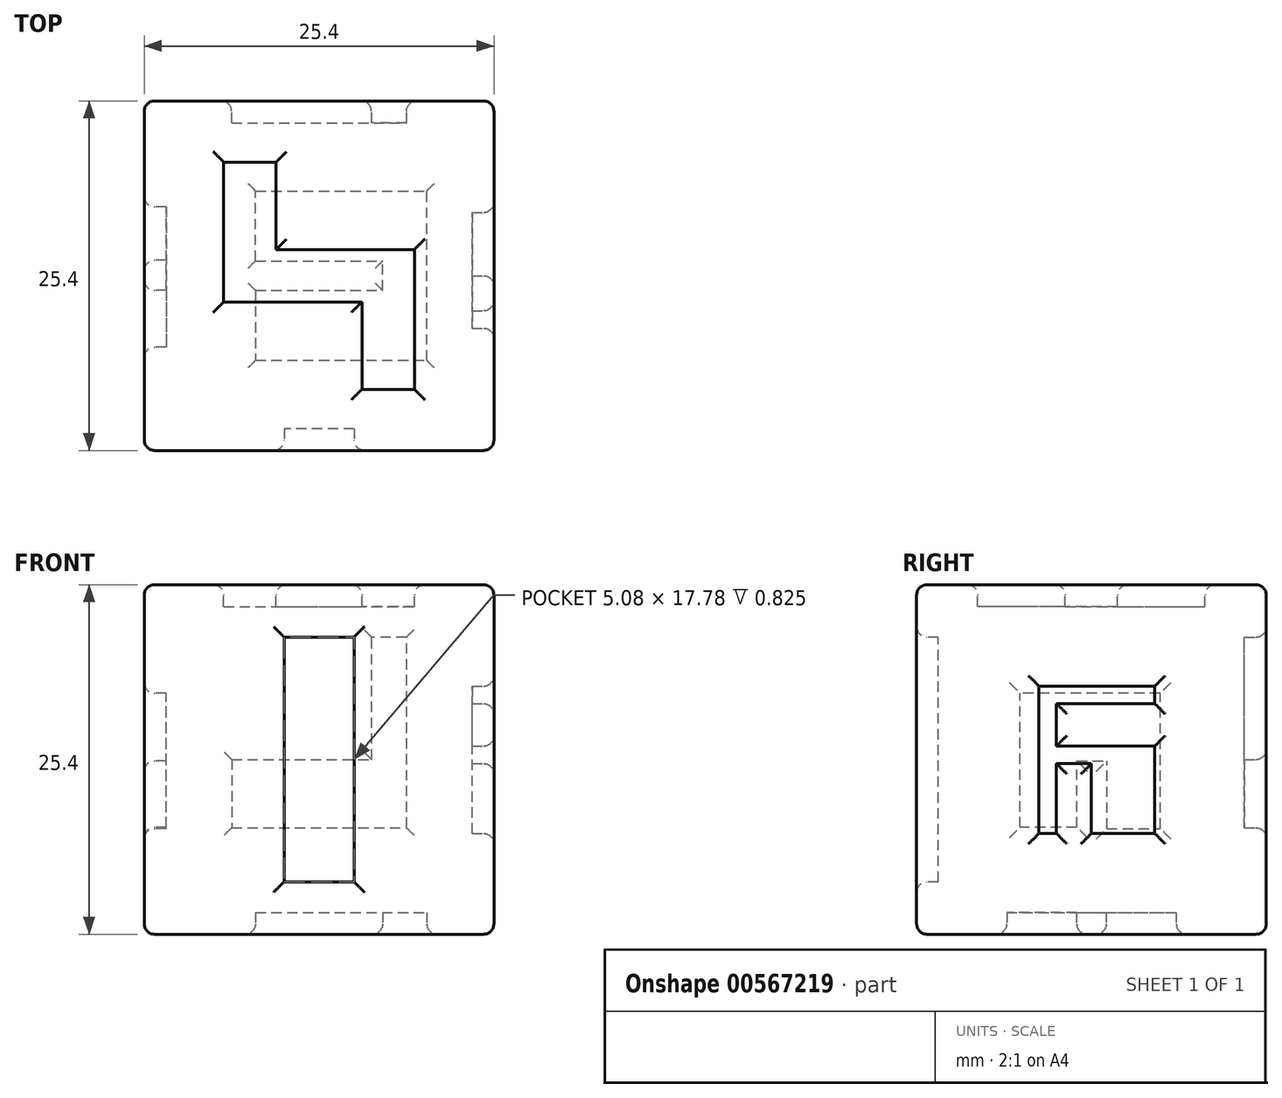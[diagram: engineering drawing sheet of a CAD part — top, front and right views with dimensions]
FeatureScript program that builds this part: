
annotation { "Feature Type Name" : "Feature", "Feature Type Description" : "" }
export const myFeature = defineFeature(function(context is Context, id is Id, definition is map)
    precondition{}
    {
        {
            var Q0;
            Q0=qCreatedBy(makeId("Top.planeOp"),FACE);
            var sketch = newSketch(context, id + "F0", { "sketchPlane" : qUnion([Q0])});
            skLineSegment(sketch, "E0.bottom", {"start": v(12.7, -12.7) * mm, "end": v(-12.7, -12.7) * mm});
            skLineSegment(sketch, "E0.top", {"start": v(12.7, 12.7) * mm, "end": v(-12.7, 12.7) * mm});
            skLineSegment(sketch, "E0.left", {"start": v(12.7, -12.7) * mm, "end": v(12.7, 12.7) * mm});
            skLineSegment(sketch, "E0.right", {"start": v(-12.7, -12.7) * mm, "end": v(-12.7, 12.7) * mm});
            skPoint(sketch, "E0.middle", {"position": v(0, 0) * mm});
            skSolve(sketch);
        }
        {
            var Q0;
            Q0=makeQuery(id+"F0.imprint","IMPRINT",FACE,{"disambiguationData":[TD([[makeQuery(id+"F0.imprint","IMPRINT",EDGE,{"derivedFrom":sQuery(id+"F0.wireOp",EDGE,"E0.bottom")}),-1.0]])]});
            extrude(context, id + "F1", {"entities" : qUnion([Q0]), "depth" : 25.4 * mm, "offsetDistance" : 25.4 * mm});
        }
        {
            var Q0;
            Q0=makeQuery(id+"F1.opExtrude","SWEPT_FACE",FACE,{"disambiguationData":[OSD([sQuery(id+"F0.wireOp",EDGE,"E0.bottom")])]});
            var sketch = newSketch(context, id + "F2", { "sketchPlane" : qUnion([Q0])});
            skLineSegment(sketch, "E1.bottom", {"start": v(2.54, 3.8) * mm, "end": v(-2.54, 3.8) * mm});
            skLineSegment(sketch, "E1.top", {"start": v(2.54, 21.59) * mm, "end": v(-2.54, 21.59) * mm});
            skLineSegment(sketch, "E1.left", {"start": v(2.54, 3.8) * mm, "end": v(2.54, 21.59) * mm});
            skLineSegment(sketch, "E1.right", {"start": v(-2.54, 3.8) * mm, "end": v(-2.54, 21.59) * mm});
            skPoint(sketch, "E1.middle", {"position": v(0, 12.7) * mm});
            skPoint(sketch, "E1.middle.positionSnap0", {"position": v(12.7, 12.7) * mm});
            skPoint(sketch, "E1.middle.positionSnap1", {"position": v(0, 0) * mm});
            skPoint(sketch, "E1.centerSnap0", {"position": v(12.7, 12.7) * mm});
            skPoint(sketch, "E1.centerSnap1", {"position": v(0, 0) * mm});
            skSolve(sketch);
        }
        {
            var Q0;
            Q0=makeQuery(id+"F1.opExtrude","CAP_FACE",FACE,{"disambiguationData":[OSD([sQuery(id+"F0.wireOp",EDGE,"E0.bottom"),sQuery(id+"F0.wireOp",EDGE,"E0.top"),sQuery(id+"F0.wireOp",EDGE,"E0.left"),sQuery(id+"F0.wireOp",EDGE,"E0.right")])],"isStart":false});
            var sketch = newSketch(context, id + "F3", { "sketchPlane" : qUnion([Q0])});
            skLineSegment(sketch, "E2.bottom", {"start": v(-6.93, -1.9) * mm, "end": v(3.12, -1.9) * mm});
            skLineSegment(sketch, "E2.top", {"start": v(-3.12, 1.9) * mm, "end": v(6.93, 1.9) * mm});
            skLineSegment(sketch, "E2.left", {"start": v(-6.93, -1.9) * mm, "end": v(-6.93, 1.9) * mm});
            skLineSegment(sketch, "E2.right", {"start": v(6.93, -1.9) * mm, "end": v(6.93, 1.9) * mm});
            skPoint(sketch, "E2.middle", {"position": v(0, 0) * mm});
            skLineSegment(sketch, "E3.top", {"start": v(-6.93, 8.26) * mm, "end": v(-3.12, 8.26) * mm});
            skLineSegment(sketch, "E3.left", {"start": v(-6.93, 1.9) * mm, "end": v(-6.93, 8.26) * mm});
            skLineSegment(sketch, "E3.right", {"start": v(-3.12, 1.9) * mm, "end": v(-3.12, 8.26) * mm});
            skLineSegment(sketch, "E4.top", {"start": v(6.93, -8.26) * mm, "end": v(3.12, -8.26) * mm});
            skLineSegment(sketch, "E4.left", {"start": v(6.93, -1.9) * mm, "end": v(6.93, -8.26) * mm});
            skLineSegment(sketch, "E4.right", {"start": v(3.12, -1.9) * mm, "end": v(3.12, -8.26) * mm});
            skSolve(sketch);
        }
        {
            var Q0;
            Q0=makeQuery(id+"F1.opExtrude","SWEPT_FACE",FACE,{"disambiguationData":[OSD([sQuery(id+"F0.wireOp",EDGE,"E0.top")])]});
            var sketch = newSketch(context, id + "F4", { "sketchPlane" : qUnion([Q0])});
            skPoint(sketch, "E5.firstSnap0", {"position": v(12.7, 12.7) * mm});
            skLineSegment(sketch, "E5.bottom", {"start": v(6.35, 12.7) * mm, "end": v(-3.81, 12.7) * mm});
            skLineSegment(sketch, "E5.top", {"start": v(6.35, 7.74) * mm, "end": v(-6.35, 7.74) * mm});
            skLineSegment(sketch, "E5.left", {"start": v(6.35, 12.7) * mm, "end": v(6.35, 7.74) * mm});
            skLineSegment(sketch, "E5.right", {"start": v(-6.35, 12.7) * mm, "end": v(-6.35, 7.74) * mm});
            skLineSegment(sketch, "E6.top", {"start": v(-6.35, 21.6) * mm, "end": v(-3.81, 21.6) * mm});
            skLineSegment(sketch, "E6.left", {"start": v(-6.35, 12.7) * mm, "end": v(-6.35, 21.6) * mm});
            skLineSegment(sketch, "E6.right", {"start": v(-3.81, 12.7) * mm, "end": v(-3.81, 21.6) * mm});
            skSolve(sketch);
        }
        {
            var Q0;
            Q0=makeQuery(id+"F1.opExtrude","CAP_FACE",FACE,{"disambiguationData":[OSD([sQuery(id+"F0.wireOp",EDGE,"E0.bottom"),sQuery(id+"F0.wireOp",EDGE,"E0.top"),sQuery(id+"F0.wireOp",EDGE,"E0.left"),sQuery(id+"F0.wireOp",EDGE,"E0.right")])],"isStart":true});
            var sketch = newSketch(context, id + "F5", { "sketchPlane" : qUnion([Q0])});
            skLineSegment(sketch, "E7.bottom", {"start": v(-4.62, 1.08) * mm, "end": v(4.62, 1.08) * mm});
            skLineSegment(sketch, "E7.top", {"start": v(-4.62, -1.08) * mm, "end": v(4.62, -1.08) * mm});
            skLineSegment(sketch, "E7.right", {"start": v(4.62, 1.08) * mm, "end": v(4.62, -1.08) * mm});
            skPoint(sketch, "E7.middle", {"position": v(0, 0) * mm});
            skLineSegment(sketch, "E8.top", {"start": v(-4.62, 6.16) * mm, "end": v(4.62, 6.16) * mm});
            skLineSegment(sketch, "E8.left", {"start": v(-4.62, 1.08) * mm, "end": v(-4.62, 6.16) * mm});
            skLineSegment(sketch, "E9.top", {"start": v(-4.62, -6.16) * mm, "end": v(4.62, -6.16) * mm});
            skLineSegment(sketch, "E9.left", {"start": v(-4.62, -1.08) * mm, "end": v(-4.62, -6.16) * mm});
            skLineSegment(sketch, "E10.bottom", {"start": v(4.62, 6.16) * mm, "end": v(7.82, 6.16) * mm});
            skLineSegment(sketch, "E10.top", {"start": v(4.62, -6.16) * mm, "end": v(7.82, -6.16) * mm});
            skLineSegment(sketch, "E10.right", {"start": v(7.82, 6.16) * mm, "end": v(7.82, -6.16) * mm});
            skSolve(sketch);
        }
        {
            var Q0;
            Q0=makeQuery(id+"F1.opExtrude","SWEPT_FACE",FACE,{"disambiguationData":[OSD([sQuery(id+"F0.wireOp",EDGE,"E0.left")])]});
            var sketch = newSketch(context, id + "F6", { "sketchPlane" : qUnion([Q0])});
            skLineSegment(sketch, "E11.bottom", {"start": v(4.6, 7.32) * mm, "end": v(0, 7.32) * mm});
            skLineSegment(sketch, "E11.left", {"start": v(4.6, 7.32) * mm, "end": v(4.6, 12.4) * mm});
            skLineSegment(sketch, "E11.right", {"start": v(0, 7.32) * mm, "end": v(0, 12.4) * mm});
            skLineSegment(sketch, "E12.bottom", {"start": v(-2.54, 7.32) * mm, "end": v(-3.81, 7.32) * mm});
            skLineSegment(sketch, "E12.top", {"start": v(-2.54, 18.02) * mm, "end": v(-3.81, 18.02) * mm});
            skLineSegment(sketch, "E12.left", {"start": v(-2.54, 7.32) * mm, "end": v(-2.54, 12.4) * mm});
            skLineSegment(sketch, "E12.right", {"start": v(-3.81, 7.32) * mm, "end": v(-3.81, 18.02) * mm});
            skLineSegment(sketch, "E13.bottom", {"start": v(0, 12.4) * mm, "end": v(-2.54, 12.4) * mm});
            skLineSegment(sketch, "E13.top", {"start": v(4.6, 13.67) * mm, "end": v(-2.54, 13.67) * mm});
            skLineSegment(sketch, "E13.left", {"start": v(4.6, 12.4) * mm, "end": v(4.6, 13.67) * mm});
            skLineSegment(sketch, "E14.bottom", {"start": v(-2.54, 18.02) * mm, "end": v(4.6, 18.02) * mm});
            skLineSegment(sketch, "E14.top", {"start": v(-2.54, 16.75) * mm, "end": v(4.6, 16.75) * mm});
            skLineSegment(sketch, "E14.right", {"start": v(4.6, 18.02) * mm, "end": v(4.6, 16.75) * mm});
            skLineSegment(sketch, "E15.trimOffspring", {"start": v(-2.54, 13.67) * mm, "end": v(-2.54, 16.75) * mm});
            skSolve(sketch);
        }
        {
            var Q0;
            Q0=makeQuery(id+"F1.opExtrude","SWEPT_FACE",FACE,{"disambiguationData":[OSD([sQuery(id+"F0.wireOp",EDGE,"E0.right")])]});
            var sketch = newSketch(context, id + "F7", { "sketchPlane" : qUnion([Q0])});
            skLineSegment(sketch, "E16.bottom", {"start": v(-1.12, 7.69) * mm, "end": v(-5, 7.69) * mm});
            skLineSegment(sketch, "E16.top", {"start": v(-1.12, 17.51) * mm, "end": v(-5, 17.51) * mm});
            skLineSegment(sketch, "E16.left", {"start": v(-1.12, 7.69) * mm, "end": v(-1.12, 12.6) * mm});
            skLineSegment(sketch, "E16.right", {"start": v(-5, 7.69) * mm, "end": v(-5, 17.51) * mm});
            skLineSegment(sketch, "E17.bottom", {"start": v(1.06, 7.77) * mm, "end": v(5.18, 7.77) * mm});
            skLineSegment(sketch, "E17.top", {"start": v(1.06, 17.51) * mm, "end": v(5.18, 17.51) * mm});
            skLineSegment(sketch, "E17.left", {"start": v(1.06, 7.77) * mm, "end": v(1.06, 12.6) * mm});
            skLineSegment(sketch, "E17.right", {"start": v(5.18, 7.77) * mm, "end": v(5.18, 17.51) * mm});
            skLineSegment(sketch, "E18.bottom", {"start": v(1.06, 17.51) * mm, "end": v(-1.12, 17.51) * mm});
            skLineSegment(sketch, "E18.top", {"start": v(1.06, 12.6) * mm, "end": v(-1.12, 12.6) * mm});
            skSolve(sketch);
        }
        {
            var Q0;
            Q0=makeQuery(id+"F7.imprint","IMPRINT",FACE,{"disambiguationData":[TD([[makeQuery(id+"F7.imprint","IMPRINT",EDGE,{"derivedFrom":sQuery(id+"F7.wireOp",EDGE,"E16.bottom")}),-1.0]])]});
            extrude(context, id + "F8", {"entities" : qUnion([Q0]), "operationType" : NewBodyOperationType.REMOVE, "oppositeDirection" : true, "depth" : 1.59 * mm, "offsetDistance" : 25.4 * mm});
        }
        {
            var Q0;
            Q0=makeQuery(id+"F2.imprint","IMPRINT",FACE,{"disambiguationData":[TD([[makeQuery(id+"F2.imprint","IMPRINT",EDGE,{"derivedFrom":sQuery(id+"F2.wireOp",EDGE,"E1.bottom")}),-1.0]])]});
            extrude(context, id + "F9", {"entities" : qUnion([Q0]), "operationType" : NewBodyOperationType.REMOVE, "oppositeDirection" : true, "depth" : 1.59 * mm, "offsetDistance" : 25.4 * mm});
        }
        {
            var Q0;
            Q0=makeQuery(id+"F6.imprint","IMPRINT",FACE,{"disambiguationData":[TD([[makeQuery(id+"F6.imprint","IMPRINT",EDGE,{"derivedFrom":sQuery(id+"F6.wireOp",EDGE,"E11.bottom")}),-1.0]])]});
            extrude(context, id + "F10", {"entities" : qUnion([Q0]), "operationType" : NewBodyOperationType.REMOVE, "oppositeDirection" : true, "depth" : 1.59 * mm, "offsetDistance" : 25.4 * mm});
        }
        {
            var Q0;
            Q0=makeQuery(id+"F4.imprint","IMPRINT",FACE,{"disambiguationData":[TD([[makeQuery(id+"F4.imprint","IMPRINT",EDGE,{"derivedFrom":sQuery(id+"F4.wireOp",EDGE,"E5.bottom")}),1.0]])]});
            extrude(context, id + "F11", {"entities" : qUnion([Q0]), "operationType" : NewBodyOperationType.REMOVE, "oppositeDirection" : true, "depth" : 1.59 * mm, "offsetDistance" : 25.4 * mm});
        }
        {
            var Q0;
            Q0=makeQuery(id+"F3.imprint","IMPRINT",FACE,{"disambiguationData":[TD([[makeQuery(id+"F3.imprint","IMPRINT",EDGE,{"derivedFrom":sQuery(id+"F3.wireOp",EDGE,"E2.bottom")}),1.0]])]});
            extrude(context, id + "F12", {"entities" : qUnion([Q0]), "operationType" : NewBodyOperationType.REMOVE, "oppositeDirection" : true, "depth" : 1.59 * mm, "offsetDistance" : 25.4 * mm});
        }
        {
            var Q0;
            Q0=makeQuery(id+"F5.imprint","IMPRINT",FACE,{"disambiguationData":[TD([[makeQuery(id+"F5.imprint","IMPRINT",EDGE,{"derivedFrom":sQuery(id+"F5.wireOp",EDGE,"E7.bottom")}),1.0]])]});
            extrude(context, id + "F13", {"entities" : qUnion([Q0]), "operationType" : NewBodyOperationType.REMOVE, "oppositeDirection" : true, "depth" : 1.59 * mm, "offsetDistance" : 25.4 * mm});
        }
        {
            var Q0;
            Q0=makeQuery(id+"F1.opExtrude","CAP_FACE",FACE,{"disambiguationData":[OSD([sQuery(id+"F0.wireOp",EDGE,"E0.bottom"),sQuery(id+"F0.wireOp",EDGE,"E0.top"),sQuery(id+"F0.wireOp",EDGE,"E0.left"),sQuery(id+"F0.wireOp",EDGE,"E0.right")])],"isStart":false});
            var Q1;
            Q1=makeQuery(id+"F1.opExtrude","SWEPT_FACE",FACE,{"disambiguationData":[OSD([sQuery(id+"F0.wireOp",EDGE,"E0.bottom")])]});
            var Q2;
            Q2=makeQuery(id+"F1.opExtrude","SWEPT_FACE",FACE,{"disambiguationData":[OSD([sQuery(id+"F0.wireOp",EDGE,"E0.left")])]});
            var Q3;
            Q3=makeQuery(id+"F1.opExtrude","SWEPT_FACE",FACE,{"disambiguationData":[OSD([sQuery(id+"F0.wireOp",EDGE,"E0.top")])]});
            var Q4;
            Q4=makeQuery(id+"F1.opExtrude","SWEPT_FACE",FACE,{"disambiguationData":[OSD([sQuery(id+"F0.wireOp",EDGE,"E0.right")])]});
            var Q5;
            Q5=makeQuery(id+"F1.opExtrude","CAP_FACE",FACE,{"disambiguationData":[OSD([sQuery(id+"F0.wireOp",EDGE,"E0.bottom"),sQuery(id+"F0.wireOp",EDGE,"E0.top"),sQuery(id+"F0.wireOp",EDGE,"E0.left"),sQuery(id+"F0.wireOp",EDGE,"E0.right")])],"isStart":true});
            fillet(context, id + "F14", {"entities" : qUnion([Q0, Q1, Q2, Q3, Q4, Q5]), "radius" : 0.76 * mm, "tangentPropagation" : true, "allowEdgeOverflow" : false});
        }
    });
